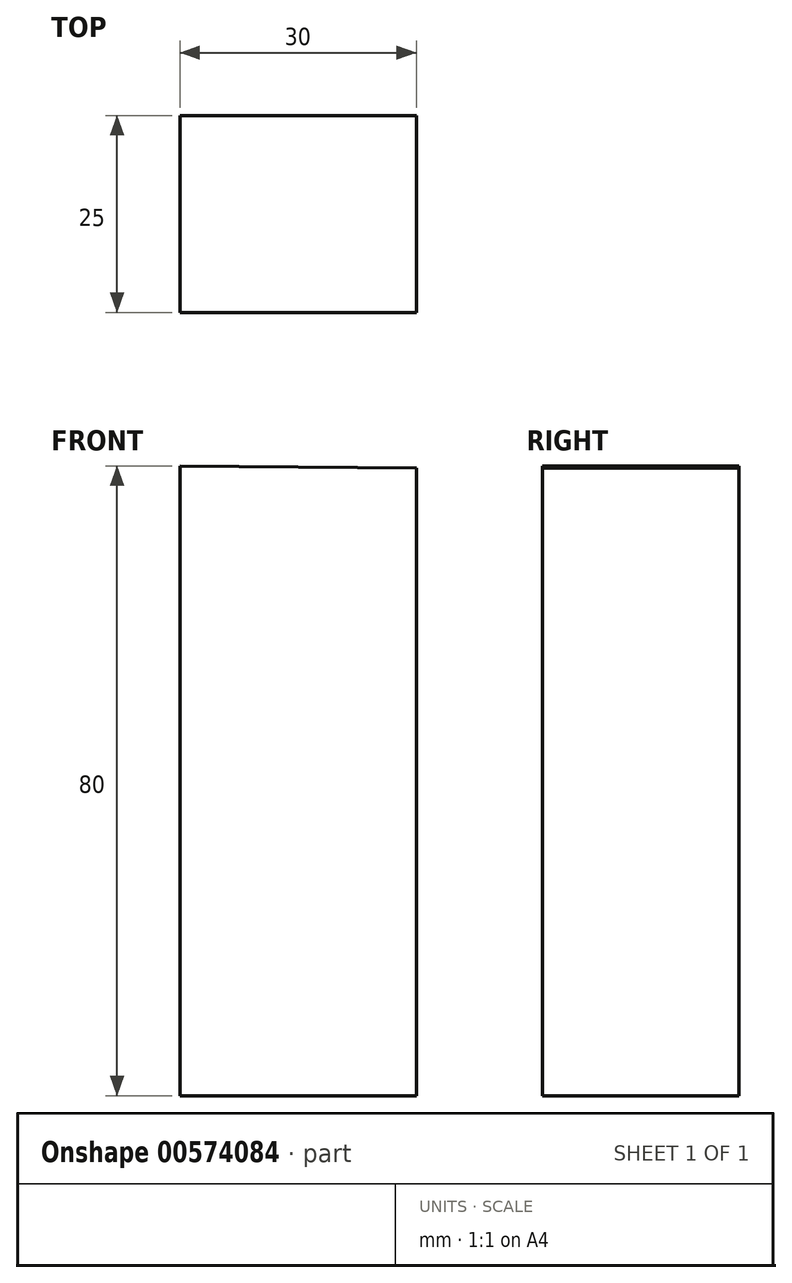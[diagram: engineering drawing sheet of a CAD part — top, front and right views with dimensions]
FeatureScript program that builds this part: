
annotation { "Feature Type Name" : "Feature", "Feature Type Description" : "" }
export const myFeature = defineFeature(function(context is Context, id is Id, definition is map)
    precondition{}
    {
        {
            var Q0;
            Q0=qCreatedBy(makeId("Front.planeOp"),FACE);
            var sketch = newSketch(context, id + "F0", { "sketchPlane" : qUnion([Q0])});
            skLineSegment(sketch, "E0", {"start": v(-31.45, 40.57) * mm, "end": v(-31.45, -39.43) * mm});
            skLineSegment(sketch, "E1", {"start": v(-31.45, -39.43) * mm, "end": v(-1.45, -39.43) * mm});
            skLineSegment(sketch, "E2", {"start": v(-1.45, -39.43) * mm, "end": v(-1.45, 40.28) * mm});
            skLineSegment(sketch, "E3", {"start": v(-1.45, 40.28) * mm, "end": v(-31.45, 40.57) * mm});
            skSolve(sketch);
        }
        {
            var Q0;
            Q0 = qSketchRegion(id + "F0", true);
            extrude(context, id + "F1", {"entities" : qUnion([Q0]), "depth" : 25 * mm, "offsetDistance" : 25 * mm});
        }
    });
